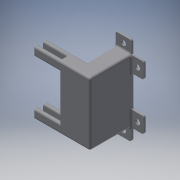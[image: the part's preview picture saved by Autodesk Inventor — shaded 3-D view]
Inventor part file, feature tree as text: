
AUTODESK INVENTOR PART (.ipt)
format: ipt  version: 2018 (Build 220112000, 112)  size: 288,256 bytes
history: native  units: mm
features: reference x18, extrude x5, sketch x5, other x4, fillet x2
ambient origin geometry x8: Origin, YZ Plane, XZ Plane, XY Plane, X Axis, Y Axis, Z Axis, Center Point
bodies: Solid1 (feature_tree)
feature tree (34):
  extrude  "Extrusion1"  Depth=2.0mm
  extrude  "Extrusion2"  Depth=2.0mm
  extrude  "Extrusion3"  Depth=32.004mm TaperAngle=0.0deg
  extrude  "Extrusion4"  Depth=32.004mm
  extrude  "Extrusion5"  Depth=1.0mm TaperAngle=0.0deg
  fillet  "Fillet1"  Radius=2.5mm
  fillet  "Fillet2"  Radius=2.5mm
  sketch  "Sketch1"  dims[d0=25.0mm d1=2.0mm]
  reference  "Reference1"
  reference  "Reference2"
  reference  "Reference3"
  reference  "Reference4"
  reference  "Reference5"
  reference  "Reference6"
  reference  "Reference7"
  reference  "Reference8"
  reference  "Reference9"
  reference  "Reference10"
  reference  "Reference11"
  reference  "Reference12"
  reference  "Reference13"
  sketch  "Sketch2"  dims[d2=2.0mm d3=20.3mm]
  reference  "Reference14"
  reference  "Reference15"
  reference  "Reference16"
  sketch  "Sketch3"  dims[d4=8.0mm d5=32.004mm d6=0.0mm]
  reference  "Reference17"
  sketch  "Sketch4"  dims[d7=32.004mm d8=0.0mm d9=6.35mm]
  sketch  "Sketch5"  dims[d10=6.35mm d11=1.0mm d12=0.0mm d13=2.5mm d14=2.5mm d15=1.0mm d16=0.0mm d17=32.004mm d18=0.0mm d19=1.0mm d20=1.0mm d21=6.35mm d22=8.0mm d23=8.0mm d24=2.5mm d25=2.5mm d26=2.5mm d27=2.5mm]
  reference  "Reference18"
  other  "<userpath>\OneDrive\Documents\Inventor\TSA\2018\Animatronics\Tortoise\AssemblyTURTLE.iam"
  other  "AssemblyTURTLE.iam"
  other  "servo (2):3"
  other  "Frame:1"
